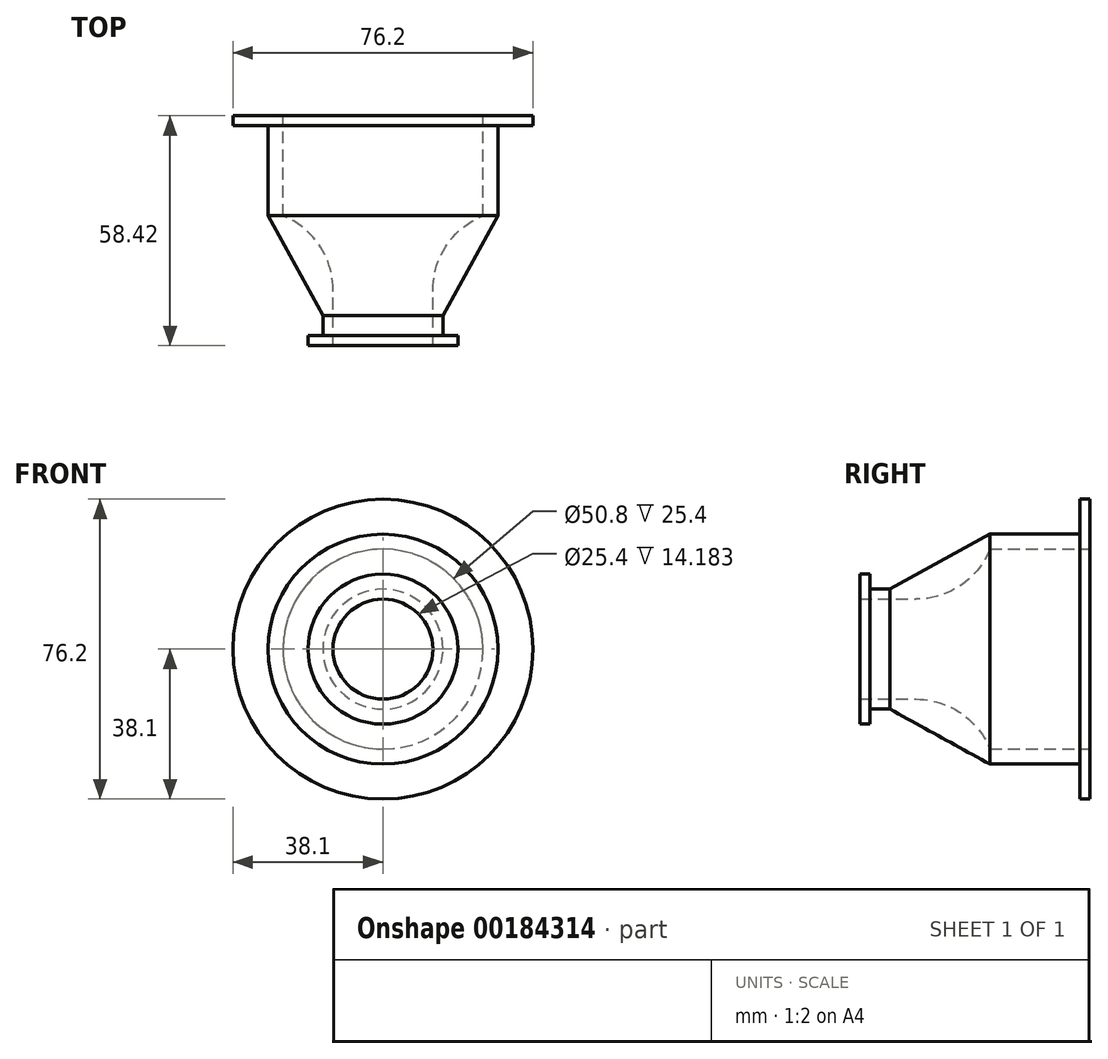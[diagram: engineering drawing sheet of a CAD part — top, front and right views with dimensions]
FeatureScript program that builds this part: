
annotation { "Feature Type Name" : "Feature", "Feature Type Description" : "" }
export const myFeature = defineFeature(function(context is Context, id is Id, definition is map)
    precondition{}
    {
        {
            var Q0;
            Q0=qCreatedBy(makeId("Front.planeOp"),FACE);
            var sketch = newSketch(context, id + "F0", { "sketchPlane" : qUnion([Q0])});
            skCircle(sketch, "E0", {"center": v(0, 0) * mm, "radius": 38.1 * mm});
            skCircle(sketch, "E1", {"center": v(0, 0) * mm, "radius": 29.21 * mm});
            skCircle(sketch, "E2", {"center": v(0, 0) * mm, "radius": 25.4 * mm});
            skSolve(sketch);
        }
        {
            var Q0;
            Q0=makeQuery(id+"F0.imprint","IMPRINT",FACE,{"disambiguationData":[TD([[makeQuery(id+"F0.imprint","IMPRINT",EDGE,{"derivedFrom":sQuery(id+"F0.wireOp",EDGE,"E1")}),1.0]])]});
            extrude(context, id + "F1", {"entities" : qUnion([Q0]), "depth" : 25.4 * mm});
        }
        {
            var Q0;
            Q0=makeQuery(id+"F0.imprint","IMPRINT",FACE,{"disambiguationData":[TD([[makeQuery(id+"F0.imprint","IMPRINT",EDGE,{"derivedFrom":sQuery(id+"F0.wireOp",EDGE,"E0")}),1.0]])]});
            extrude(context, id + "F2", {"entities" : qUnion([Q0]), "operationType" : NewBodyOperationType.ADD, "depth" : 2.54 * mm});
        }
        {
            var Q0;
            Q0=qCreatedBy(makeId("Front.planeOp"),FACE);
            cPlane(context, id + "F3", {"entities" : qUnion([Q0]), "cplaneType" : CPlaneType.OFFSET, "offset" : 50.8 * mm, "width" : 152.4 * mm, "height" : 152.4 * mm});
        }
        {
            var Q0;
            Q0=qCreatedBy(id+"F3.planeOp",FACE);
            var sketch = newSketch(context, id + "F4", { "sketchPlane" : qUnion([Q0])});
            skCircle(sketch, "E3", {"center": v(0, 0) * mm, "radius": 15.24 * mm});
            skSolve(sketch);
        }
        {
            var Q0;
            Q0=makeQuery(id+"F1.opExtrude","CAP_FACE",FACE,{"disambiguationData":[OSD([sQuery(id+"F0.wireOp",EDGE,"E1"),sQuery(id+"F0.wireOp",EDGE,"E2")])],"isStart":false});
            var sketch = newSketch(context, id + "F5", { "sketchPlane" : qUnion([Q0])});
            skCircle(sketch, "E4", {"center": v(0, 0) * mm, "radius": 29.21 * mm});
            skSolve(sketch);
        }
        {
            var Q1;
            Q1 = qSketchRegion(id + "F5", true);
            var Q2;
            Q2=makeQuery(id+"F4.imprint","IMPRINT",FACE,{"disambiguationData":[TD([[makeQuery(id+"F4.imprint","IMPRINT",EDGE,{"derivedFrom":sQuery(id+"F4.wireOp",EDGE,"E3")}),1.0]])]});
            loft(context, id + "F6", {"operationType" : NewBodyOperationType.ADD, "sheetProfilesArray" : [{ "sheetProfileEntities" : qUnion([Q1]) }, { "sheetProfileEntities" : qUnion([Q2]) }]});
        }
        {
            var Q0;
            Q0=makeQuery(id+"F6.opLoft","CAP_FACE",FACE,{"disambiguationData":[OSD([makeQuery(id+"F4.imprint","IMPRINT",FACE,{"disambiguationData":[TD([[makeQuery(id+"F4.imprint","IMPRINT",EDGE,{"derivedFrom":sQuery(id+"F4.wireOp",EDGE,"E3")}),1.0]])]})])],"isStart":true});
            var sketch = newSketch(context, id + "F7", { "sketchPlane" : qUnion([Q0])});
            skCircle(sketch, "E5", {"center": v(0, 0) * mm, "radius": 12.7 * mm});
            skCircle(sketch, "E6", {"center": v(0, 0) * mm, "radius": 15.24 * mm});
            skSolve(sketch);
        }
        {
            var Q0;
            Q0 = qSketchRegion(id + "F7", true);
            extrude(context, id + "F8", {"entities" : qUnion([Q0]), "operationType" : NewBodyOperationType.ADD, "depth" : 7.62 * mm});
        }
        {
            var Q0;
            Q0=makeQuery(id+"F8.opExtrude","CAP_FACE",FACE,{"disambiguationData":[OSD([sQuery(id+"F7.wireOp",EDGE,"E5"),sQuery(id+"F7.wireOp",EDGE,"E6")])],"isStart":false});
            var sketch = newSketch(context, id + "F9", { "sketchPlane" : qUnion([Q0])});
            skCircle(sketch, "E7", {"center": v(0, 0) * mm, "radius": 15.24 * mm});
            skCircle(sketch, "E8", {"center": v(0, 0) * mm, "radius": 19.05 * mm});
            skSolve(sketch);
        }
        {
            var Q0;
            Q0 = qSketchRegion(id + "F9", true);
            extrude(context, id + "F10", {"entities" : qUnion([Q0]), "operationType" : NewBodyOperationType.ADD, "oppositeDirection" : true, "depth" : 2.54 * mm});
        }
        {
            var Q0;
            Q0=makeQuery(id+"F6.opLoft","CAP_FACE",FACE,{"disambiguationData":[OSD([makeQuery(id+"F4.imprint","IMPRINT",FACE,{"disambiguationData":[TD([[makeQuery(id+"F4.imprint","IMPRINT",EDGE,{"derivedFrom":sQuery(id+"F4.wireOp",EDGE,"E3")}),1.0]])]})])],"isStart":true});
            extrude(context, id + "F11", {"entities" : qUnion([Q0]), "operationType" : NewBodyOperationType.REMOVE, "oppositeDirection" : true, "depth" : 57.66 * mm});
        }
        {
            var Q0;
            Q0=makeQuery(id+"F11.boolean.opBoolean","INTERSECT",EDGE,{"derivedFrom":[makeQuery(id+"F6.opLoft","CAP_FACE",FACE,{"disambiguationData":[OSD([makeQuery(id+"F5.imprint","IMPRINT",FACE,{"disambiguationData":[TD([[makeQuery(id+"F5.imprint","IMPRINT",EDGE,{"derivedFrom":makeQuery(id+"F1.opExtrude","CAP_EDGE",EDGE,{"disambiguationData":[OSD([sQuery(id+"F0.wireOp",EDGE,"E2")])],"isStart":false})}),1.0]])]})])],"isStart":true}),makeQuery(id+"F11.opExtrude","SWEPT_FACE",FACE,{"disambiguationData":[OSD([sQuery(id+"F7.wireOp",EDGE,"E5")])]})]});
            fillet(context, id + "F12", {"entities" : qUnion([Q0]), "radius" : 20.32 * mm, "tangentPropagation" : true, "allowEdgeOverflow" : false});
        }
    });
